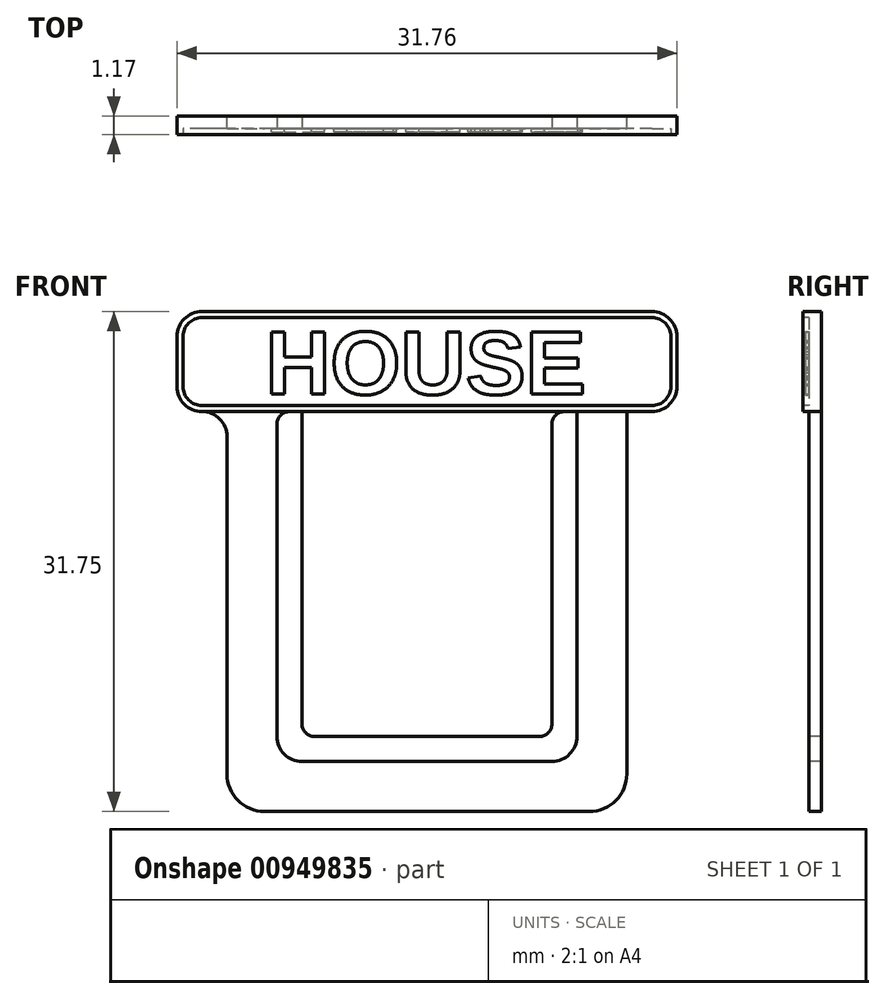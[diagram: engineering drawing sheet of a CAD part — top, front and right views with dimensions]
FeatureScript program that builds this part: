
annotation { "Feature Type Name" : "Feature", "Feature Type Description" : "" }
export const myFeature = defineFeature(function(context is Context, id is Id, definition is map)
    precondition{}
    {
        {
            var Q0;
            Q0=qCreatedBy(makeId("Front.planeOp"),FACE);
            var sketch = newSketch(context, id + "F0", { "sketchPlane" : qUnion([Q0])});
            skLineSegment(sketch, "E0.bottom", {"start": v(12.7, 12.7) * mm, "end": v(-12.7, 12.7) * mm});
            skLineSegment(sketch, "E0.top", {"start": v(12.7, -12.7) * mm, "end": v(-12.7, -12.7) * mm});
            skLineSegment(sketch, "E0.left", {"start": v(12.7, 12.7) * mm, "end": v(12.7, -12.7) * mm});
            skLineSegment(sketch, "E0.right", {"start": v(-12.7, 12.7) * mm, "end": v(-12.7, -12.7) * mm});
            skPoint(sketch, "E0.middle", {"position": v(0, 0) * mm});
            skSolve(sketch);
        }
        {
            var Q0;
            Q0=makeQuery(id+"F0.imprint","IMPRINT",FACE,{"disambiguationData":[TD([[makeQuery(id+"F0.imprint","IMPRINT",EDGE,{"derivedFrom":sQuery(id+"F0.wireOp",EDGE,"E0.bottom")}),1.0]])]});
            extrude(context, id + "F1", {"entities" : qUnion([Q0]), "depth" : 0.8 * mm, "offsetDistance" : 25.4 * mm});
        }
        {
            var Q0;
            Q0=makeQuery(id+"F1.opExtrude","SWEPT_EDGE",EDGE,{"disambiguationData":[OSD([sQuery(id+"F0.wireOp",EDGE,"E0.top"),sQuery(id+"F0.wireOp",EDGE,"E0.left")])]});
            var Q1;
            Q1=makeQuery(id+"F1.opExtrude","SWEPT_EDGE",EDGE,{"disambiguationData":[OSD([sQuery(id+"F0.wireOp",EDGE,"E0.top"),sQuery(id+"F0.wireOp",EDGE,"E0.right")])]});
            fillet(context, id + "F2", {"entities" : qUnion([Q0, Q1]), "radius" : 2.38 * mm, "tangentPropagation" : true, "allowEdgeOverflow" : false});
        }
        {
            var Q0;
            Q0=makeQuery(id+"F1.opExtrude","CAP_FACE",FACE,{"disambiguationData":[OSD([sQuery(id+"F0.wireOp",EDGE,"E0.bottom"),sQuery(id+"F0.wireOp",EDGE,"E0.top"),sQuery(id+"F0.wireOp",EDGE,"E0.left"),sQuery(id+"F0.wireOp",EDGE,"E0.right")])],"isStart":false});
            var sketch = newSketch(context, id + "F3", { "sketchPlane" : qUnion([Q0])});
            skLineSegment(sketch, "E1.bottom", {"start": v(9.52, 12.7) * mm, "end": v(-9.53, 12.7) * mm});
            skLineSegment(sketch, "E1.top", {"start": v(9.53, -9.53) * mm, "end": v(-9.52, -9.53) * mm});
            skLineSegment(sketch, "E1.left", {"start": v(9.52, 12.7) * mm, "end": v(9.53, -9.53) * mm});
            skLineSegment(sketch, "E1.right", {"start": v(-9.53, 12.7) * mm, "end": v(-9.52, -9.53) * mm});
            skPoint(sketch, "E1.middle", {"position": v(0, 0) * mm});
            skSolve(sketch);
        }
        {
            var Q0;
            Q0=makeQuery(id+"F3.imprint","IMPRINT",FACE,{"disambiguationData":[TD([[makeQuery(id+"F3.imprint","IMPRINT",EDGE,{"derivedFrom":sQuery(id+"F3.wireOp",EDGE,"E1.bottom")}),1.0]])]});
            extrude(context, id + "F4", {"entities" : qUnion([Q0]), "operationType" : NewBodyOperationType.REMOVE, "oppositeDirection" : true, "depth" : 4.93 * mm, "offsetDistance" : 25.4 * mm});
        }
        {
            var Q0;
            Q0=makeQuery(id+"F1.opExtrude","CAP_FACE",FACE,{"disambiguationData":[OSD([sQuery(id+"F0.wireOp",EDGE,"E0.bottom"),sQuery(id+"F0.wireOp",EDGE,"E0.top"),sQuery(id+"F0.wireOp",EDGE,"E0.left"),sQuery(id+"F0.wireOp",EDGE,"E0.right")])],"isStart":false});
            var sketch = newSketch(context, id + "F5", { "sketchPlane" : qUnion([Q0])});
            skLineSegment(sketch, "E2.bottom", {"start": v(-15.88, 12.7) * mm, "end": v(15.88, 12.7) * mm});
            skLineSegment(sketch, "E2.top", {"start": v(-15.88, 19.05) * mm, "end": v(15.88, 19.05) * mm});
            skLineSegment(sketch, "E2.left", {"start": v(-15.88, 12.7) * mm, "end": v(-15.88, 19.05) * mm});
            skLineSegment(sketch, "E2.right", {"start": v(15.87, 12.7) * mm, "end": v(15.87, 19.05) * mm});
            skSolve(sketch);
        }
        {
            var Q0;
            Q0=makeQuery(id+"F5.imprint","IMPRINT",FACE,{"disambiguationData":[TD([[makeQuery(id+"F5.imprint","IMPRINT",EDGE,{"derivedFrom":sQuery(id+"F5.wireOp",EDGE,"E2.top")}),-1.0]])]});
            extrude(context, id + "F6", {"entities" : qUnion([Q0]), "operationType" : NewBodyOperationType.ADD, "oppositeDirection" : true, "depth" : 0.8 * mm, "offsetDistance" : 25.4 * mm});
        }
        {
            var Q0;
            Q0=makeQuery(id+"F6.opExtrude","SWEPT_EDGE",EDGE,{"disambiguationData":[OSD([sQuery(id+"F5.wireOp",EDGE,"E2.top"),sQuery(id+"F5.wireOp",EDGE,"E2.left")])]});
            var Q1;
            Q1=makeQuery(id+"F6.opExtrude","SWEPT_EDGE",EDGE,{"disambiguationData":[OSD([sQuery(id+"F5.wireOp",EDGE,"E2.top"),sQuery(id+"F5.wireOp",EDGE,"E2.right")])]});
            var Q2;
            Q2=makeQuery(id+"F6.opExtrude","SWEPT_EDGE",EDGE,{"disambiguationData":[OSD([sQuery(id+"F5.wireOp",EDGE,"E2.bottom"),sQuery(id+"F5.wireOp",EDGE,"E2.right")])]});
            var Q3;
            Q3=makeQuery(id+"F1.opExtrude","SWEPT_EDGE",EDGE,{"disambiguationData":[OSD([sQuery(id+"F0.wireOp",EDGE,"E0.bottom"),sQuery(id+"F0.wireOp",EDGE,"E0.left")])]});
            var Q4;
            Q4=makeQuery(id+"F6.opExtrude","SWEPT_EDGE",EDGE,{"disambiguationData":[OSD([sQuery(id+"F5.wireOp",EDGE,"E2.bottom"),sQuery(id+"F5.wireOp",EDGE,"E2.left")])]});
            var Q5;
            Q5=makeQuery(id+"F1.opExtrude","SWEPT_EDGE",EDGE,{"disambiguationData":[OSD([sQuery(id+"F0.wireOp",EDGE,"E0.bottom"),sQuery(id+"F0.wireOp",EDGE,"E0.right")])]});
            fillet(context, id + "F7", {"entities" : qUnion([Q0, Q1, Q2, Q3, Q4, Q5]), "radius" : 1.59 * mm, "tangentPropagation" : true, "allowEdgeOverflow" : false});
        }
        {
            var Q0;
            Q0=makeQuery(id+"F4.boolean.opBoolean","COPY",EDGE,{"derivedFrom":makeQuery(id+"F4.opExtrude","SWEPT_EDGE",EDGE,{"disambiguationData":[OSD([sQuery(id+"F3.wireOp",EDGE,"E1.top"),sQuery(id+"F3.wireOp",EDGE,"E1.right")])]})});
            var Q1;
            Q1=makeQuery(id+"F4.boolean.opBoolean","COPY",EDGE,{"derivedFrom":makeQuery(id+"F4.opExtrude","SWEPT_EDGE",EDGE,{"disambiguationData":[OSD([sQuery(id+"F3.wireOp",EDGE,"E1.top"),sQuery(id+"F3.wireOp",EDGE,"E1.left")])]})});
            fillet(context, id + "F8", {"entities" : qUnion([Q0, Q1]), "radius" : 1.59 * mm, "tangentPropagation" : true, "allowEdgeOverflow" : false});
        }
        {
            var Q0;
            Q0=makeQuery(id+"F6.boolean.opBoolean","MERGE",FACE,{"derivedFrom":[makeQuery(id+"F1.opExtrude","CAP_FACE",FACE,{"disambiguationData":[OSD([sQuery(id+"F0.wireOp",EDGE,"E0.bottom"),sQuery(id+"F0.wireOp",EDGE,"E0.top"),sQuery(id+"F0.wireOp",EDGE,"E0.left"),sQuery(id+"F0.wireOp",EDGE,"E0.right")])],"isStart":false}),makeQuery(id+"F6.opExtrude","CAP_FACE",FACE,{"disambiguationData":[OSD([sQuery(id+"F5.wireOp",EDGE,"E2.bottom"),sQuery(id+"F5.wireOp",EDGE,"E2.top"),sQuery(id+"F5.wireOp",EDGE,"E2.left"),sQuery(id+"F5.wireOp",EDGE,"E2.right")])],"isStart":true})]});
            var sketch = newSketch(context, id + "F9", { "sketchPlane" : qUnion([Q0])});
            skLineSegment(sketch, "E3.bottom", {"start": v(-7.94, 12.7) * mm, "end": v(7.94, 12.7) * mm});
            skLineSegment(sketch, "E3.top", {"start": v(-7.94, -7.94) * mm, "end": v(7.94, -7.94) * mm});
            skLineSegment(sketch, "E3.left", {"start": v(-7.94, 12.7) * mm, "end": v(-7.94, -7.94) * mm});
            skLineSegment(sketch, "E3.right", {"start": v(7.94, 12.7) * mm, "end": v(7.94, -7.94) * mm});
            skSolve(sketch);
        }
        {
            var Q0;
            Q0=makeQuery(id+"F9.imprint","IMPRINT",FACE,{"disambiguationData":[TD([[makeQuery(id+"F9.imprint","IMPRINT",EDGE,{"derivedFrom":sQuery(id+"F9.wireOp",EDGE,"E3.bottom")}),1.0]])]});
            extrude(context, id + "F10", {"entities" : qUnion([Q0]), "operationType" : NewBodyOperationType.ADD, "oppositeDirection" : true, "depth" : 0.8 * mm, "offsetDistance" : 25.4 * mm});
        }
        {
            var Q0;
            Q0=makeQuery(id+"F10.opExtrude","SWEPT_EDGE",EDGE,{"disambiguationData":[OSD([sQuery(id+"F5.wireOp",EDGE,"E2.bottom"),sQuery(id+"F9.wireOp",EDGE,"E3.bottom"),sQuery(id+"F9.wireOp",EDGE,"E3.left")])]});
            var Q1;
            Q1=makeQuery(id+"F4.boolean.opBoolean","COPY",EDGE,{"derivedFrom":makeQuery(id+"F4.opExtrude","SWEPT_EDGE",EDGE,{"disambiguationData":[OSD([sQuery(id+"F0.wireOp",EDGE,"E0.bottom"),sQuery(id+"F3.wireOp",EDGE,"E1.bottom"),sQuery(id+"F3.wireOp",EDGE,"E1.right")])]})});
            var Q2;
            Q2=makeQuery(id+"F10.opExtrude","SWEPT_EDGE",EDGE,{"disambiguationData":[OSD([sQuery(id+"F5.wireOp",EDGE,"E2.bottom"),sQuery(id+"F9.wireOp",EDGE,"E3.bottom"),sQuery(id+"F9.wireOp",EDGE,"E3.right")])]});
            var Q3;
            Q3=makeQuery(id+"F4.boolean.opBoolean","COPY",EDGE,{"derivedFrom":makeQuery(id+"F4.opExtrude","SWEPT_EDGE",EDGE,{"disambiguationData":[OSD([sQuery(id+"F0.wireOp",EDGE,"E0.bottom"),sQuery(id+"F3.wireOp",EDGE,"E1.bottom"),sQuery(id+"F3.wireOp",EDGE,"E1.left")])]})});
            fillet(context, id + "F11", {"entities" : qUnion([Q0, Q1, Q2, Q3]), "radius" : 0.8 * mm, "tangentPropagation" : true, "allowEdgeOverflow" : false});
        }
        {
            var Q0;
            Q0=makeQuery(id+"F10.opExtrude","SWEPT_EDGE",EDGE,{"disambiguationData":[OSD([sQuery(id+"F9.wireOp",EDGE,"E3.top"),sQuery(id+"F9.wireOp",EDGE,"E3.left")])]});
            var Q1;
            Q1=makeQuery(id+"F10.opExtrude","SWEPT_EDGE",EDGE,{"disambiguationData":[OSD([sQuery(id+"F9.wireOp",EDGE,"E3.top"),sQuery(id+"F9.wireOp",EDGE,"E3.right")])]});
            fillet(context, id + "F12", {"entities" : qUnion([Q0, Q1]), "radius" : 0.8 * mm, "tangentPropagation" : true, "allowEdgeOverflow" : false});
        }
        {
            var Q0;
            Q0=makeQuery(id+"F10.boolean.opBoolean","MERGE",FACE,{"derivedFrom":[makeQuery(id+"F6.boolean.opBoolean","MERGE",FACE,{"derivedFrom":[makeQuery(id+"F1.opExtrude","CAP_FACE",FACE,{"disambiguationData":[OSD([sQuery(id+"F0.wireOp",EDGE,"E0.bottom"),sQuery(id+"F0.wireOp",EDGE,"E0.top"),sQuery(id+"F0.wireOp",EDGE,"E0.left"),sQuery(id+"F0.wireOp",EDGE,"E0.right")])],"isStart":false}),makeQuery(id+"F6.opExtrude","CAP_FACE",FACE,{"disambiguationData":[OSD([sQuery(id+"F5.wireOp",EDGE,"E2.bottom"),sQuery(id+"F5.wireOp",EDGE,"E2.top"),sQuery(id+"F5.wireOp",EDGE,"E2.left"),sQuery(id+"F5.wireOp",EDGE,"E2.right")])],"isStart":true})]}),makeQuery(id+"F10.opExtrude","CAP_FACE",FACE,{"disambiguationData":[OSD([sQuery(id+"F9.wireOp",EDGE,"E3.bottom"),sQuery(id+"F9.wireOp",EDGE,"E3.top"),sQuery(id+"F9.wireOp",EDGE,"E3.left"),sQuery(id+"F9.wireOp",EDGE,"E3.right")])],"isStart":true})]});
            var sketch = newSketch(context, id + "F13", { "sketchPlane" : qUnion([Q0])});
            skArc(sketch, "E4.0", {"start": v(-14.29, 19.05) * mm, "mid": v(-15.41, 18.59) * mm, "end": v(-15.88, 17.46) * mm});
            skLineSegment(sketch, "E5.0", {"start": v(-15.88, 14.29) * mm, "end": v(-15.88, 17.46) * mm});
            skArc(sketch, "E6.0", {"start": v(-15.88, 14.29) * mm, "mid": v(-15.41, 13.16) * mm, "end": v(-14.29, 12.7) * mm});
            skLineSegment(sketch, "E7.0", {"start": v(-14.29, 19.05) * mm, "end": v(14.29, 19.05) * mm});
            skArc(sketch, "E8.0", {"start": v(15.87, 17.46) * mm, "mid": v(15.41, 18.59) * mm, "end": v(14.29, 19.05) * mm});
            skLineSegment(sketch, "E9.0", {"start": v(15.87, 14.29) * mm, "end": v(15.87, 17.46) * mm});
            skArc(sketch, "E10.0", {"start": v(14.29, 12.7) * mm, "mid": v(15.41, 13.16) * mm, "end": v(15.87, 14.29) * mm});
            skLineSegment(sketch, "E11", {"start": v(-14.29, 12.7) * mm, "end": v(14.29, 12.7) * mm});
            skSolve(sketch);
        }
        {
            var Q0;
            Q0=makeQuery(id+"F13.imprint","IMPRINT",FACE,{"disambiguationData":[TD([[makeQuery(id+"F13.imprint","IMPRINT",EDGE,{"derivedFrom":sQuery(id+"F13.wireOp",EDGE,"E4.0")}),1.0]])]});
            extrude(context, id + "F14", {"entities" : qUnion([Q0]), "operationType" : NewBodyOperationType.ADD, "depth" : 0.38 * mm, "offsetDistance" : 25.4 * mm});
        }
        {
            var Q0;
            Q0=makeQuery(id+"F14.opExtrude","CAP_FACE",FACE,{"disambiguationData":[OSD([sQuery(id+"F13.wireOp",EDGE,"E4.0"),sQuery(id+"F13.wireOp",EDGE,"E5.0"),sQuery(id+"F13.wireOp",EDGE,"E6.0"),sQuery(id+"F13.wireOp",EDGE,"E7.0"),sQuery(id+"F13.wireOp",EDGE,"E8.0"),sQuery(id+"F13.wireOp",EDGE,"E9.0"),sQuery(id+"F13.wireOp",EDGE,"E10.0"),sQuery(id+"F13.wireOp",EDGE,"E11")])],"isStart":false});
            var sketch = newSketch(context, id + "F15", { "sketchPlane" : qUnion([Q0])});
            skArc(sketch, "E12.0", {"start": v(-14.29, 19.05) * mm, "mid": v(-15.41, 18.59) * mm, "end": v(-15.88, 17.46) * mm});
            skLineSegment(sketch, "E13.0", {"start": v(-14.29, 19.05) * mm, "end": v(14.29, 19.05) * mm});
            skLineSegment(sketch, "E14.0", {"start": v(-15.88, 14.29) * mm, "end": v(-15.88, 17.46) * mm});
            skArc(sketch, "E15.0", {"start": v(-15.88, 14.29) * mm, "mid": v(-15.41, 13.16) * mm, "end": v(-14.29, 12.7) * mm});
            skLineSegment(sketch, "E16.0", {"start": v(-14.29, 12.7) * mm, "end": v(14.29, 12.7) * mm});
            skArc(sketch, "E17.0", {"start": v(14.29, 12.7) * mm, "mid": v(15.41, 13.16) * mm, "end": v(15.87, 14.29) * mm});
            skArc(sketch, "E18.0", {"start": v(15.87, 17.46) * mm, "mid": v(15.41, 18.59) * mm, "end": v(14.29, 19.05) * mm});
            skArc(sketch, "E19", {"start": v(-14.29, 18.67) * mm, "mid": v(-15.14, 18.32) * mm, "end": v(-15.5, 17.46) * mm});
            skArc(sketch, "E20", {"start": v(-15.5, 14.29) * mm, "mid": v(-15.14, 13.43) * mm, "end": v(-14.29, 13.08) * mm});
            skArc(sketch, "E21", {"start": v(15.5, 17.46) * mm, "mid": v(15.14, 18.32) * mm, "end": v(14.29, 18.67) * mm});
            skArc(sketch, "E22", {"start": v(14.29, 13.08) * mm, "mid": v(15.14, 13.43) * mm, "end": v(15.5, 14.29) * mm});
            skLineSegment(sketch, "E23", {"start": v(-14.29, 19.05) * mm, "end": v(-14.29, 12.7) * mm, "construction": true});
            skLineSegment(sketch, "E24", {"start": v(-15.88, 17.46) * mm, "end": v(15.87, 17.46) * mm, "construction": true});
            skLineSegment(sketch, "E25", {"start": v(14.29, 19.05) * mm, "end": v(14.29, 12.7) * mm, "construction": true});
            skLineSegment(sketch, "E26", {"start": v(15.87, 14.29) * mm, "end": v(-15.88, 14.29) * mm, "construction": true});
            skLineSegment(sketch, "E27", {"start": v(14.29, 18.67) * mm, "end": v(-14.29, 18.67) * mm});
            skLineSegment(sketch, "E28", {"start": v(-15.5, 17.46) * mm, "end": v(-15.5, 14.29) * mm});
            skLineSegment(sketch, "E29", {"start": v(-14.29, 13.08) * mm, "end": v(14.29, 13.08) * mm});
            skLineSegment(sketch, "E30", {"start": v(15.5, 17.46) * mm, "end": v(15.5, 14.29) * mm});
            skSolve(sketch);
        }
        {
            var Q0;
            Q0=makeQuery(id+"F15.imprint","IMPRINT",FACE,{"disambiguationData":[TD([[makeQuery(id+"F15.imprint","IMPRINT",EDGE,{"derivedFrom":sQuery(id+"F15.wireOp",EDGE,"E19")}),1.0]])]});
            var Q1;
            {var subQ0=sQuery(id+"F9.wireOp",EDGE,"E3.right");var subQ1=sQuery(id+"F9.wireOp",EDGE,"E3.top");var subQ3=sQuery(id+"F0.wireOp",EDGE,"E0.bottom");var subQ4=sQuery(id+"F9.wireOp",EDGE,"E3.left");var subQ5=makeQuery(id+"F6.opExtrude","CAP_FACE",FACE,{"disambiguationData":[OSD([sQuery(id+"F5.wireOp",EDGE,"E2.bottom"),sQuery(id+"F5.wireOp",EDGE,"E2.top"),sQuery(id+"F5.wireOp",EDGE,"E2.left"),sQuery(id+"F5.wireOp",EDGE,"E2.right")])],"isStart":true});var subQ6=makeQuery(id+"F1.opExtrude","CAP_FACE",FACE,{"disambiguationData":[OSD([subQ3,sQuery(id+"F0.wireOp",EDGE,"E0.top"),sQuery(id+"F0.wireOp",EDGE,"E0.left"),sQuery(id+"F0.wireOp",EDGE,"E0.right")])],"isStart":false});var subQ7=makeQuery(id+"F10.opExtrude","CAP_FACE",FACE,{"disambiguationData":[OSD([sQuery(id+"F9.wireOp",EDGE,"E3.bottom"),subQ1,subQ4,subQ0])],"isStart":true});Q1=makeQuery(id+"F14.boolean.opBoolean","SPLIT",FACE,{"disambiguationData":[TD([makeQuery(id+"F10.opExtrude","SWEPT_FACE",FACE,{"disambiguationData":[OSD([subQ1])]})])],"derivedFrom":makeQuery(id+"F10.boolean.opBoolean","MERGE",FACE,{"derivedFrom":[makeQuery(id+"F6.boolean.opBoolean","MERGE",FACE,{"derivedFrom":[subQ6,subQ5]}),subQ7]})});}
            extrude(context, id + "F16", {"entities" : qUnion([Q0]), "operationType" : NewBodyOperationType.REMOVE, "endBound" : BoundingType.UP_TO_SURFACE, "oppositeDirection" : true, "depth" : 25.4 * mm, "endBoundEntityFace" : qUnion([Q1]), "offsetDistance" : 25.4 * mm});
        }
        {
            var Q0;
            Q0=qCreatedBy(makeId("Front.planeOp"),FACE);
            var sketch = newSketch(context, id + "F17", { "sketchPlane" : qUnion([Q0])});
            skText(sketch, "E31", { "text": "HOUSE", "fontName": "Arimo-Bold.ttf"});
            const initialGuessF17  = {"E31": [-0.01026, 0.0138, 1, 0, 0.00412]};
            skSetInitialGuess(sketch, initialGuessF17);
            skSolve(sketch);
        }
        {
            var Q0;
            Q0=qSketchRegion(id+"F17",true);
            extrude(context, id + "F18", {"entities" : qUnion([Q0]), "operationType" : NewBodyOperationType.ADD, "depth" : 1.02 * mm, "offsetDistance" : 25.4 * mm});
        }
    });
